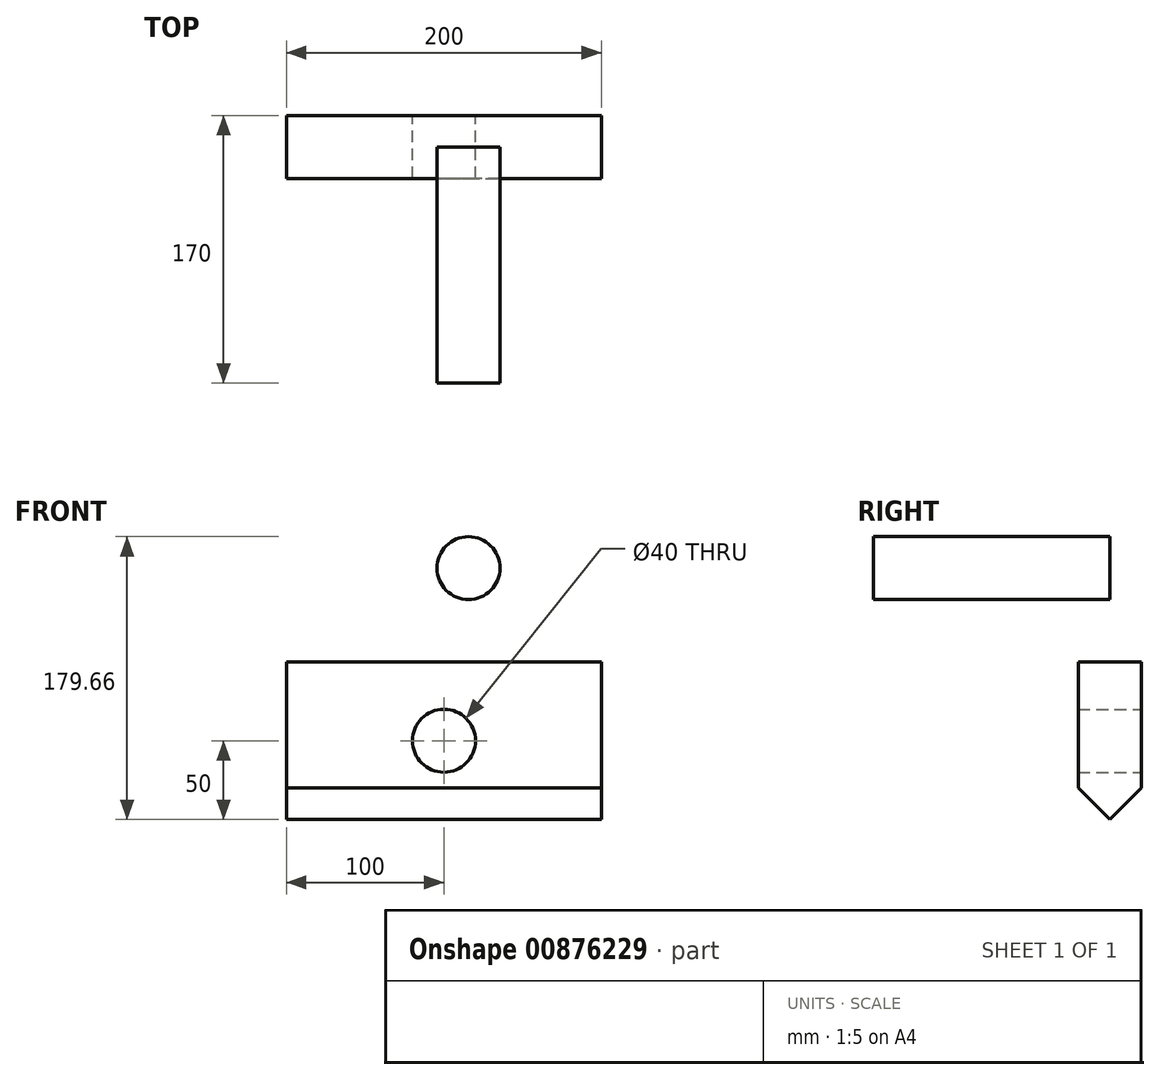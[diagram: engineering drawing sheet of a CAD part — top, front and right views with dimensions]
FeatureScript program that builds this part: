
annotation { "Feature Type Name" : "Feature", "Feature Type Description" : "" }
export const myFeature = defineFeature(function(context is Context, id is Id, definition is map)
    precondition{}
    {
        {
            var Q0;
            Q0=qCreatedBy(makeId("Front.planeOp"),FACE);
            var sketch = newSketch(context, id + "F0", { "sketchPlane" : qUnion([Q0])});
            skLineSegment(sketch, "E0.bottom", {"start": v(100, 50) * mm, "end": v(-100, 50) * mm});
            skLineSegment(sketch, "E0.top", {"start": v(100, -50) * mm, "end": v(-100, -50) * mm});
            skLineSegment(sketch, "E0.left", {"start": v(100, 50) * mm, "end": v(100, -50) * mm});
            skLineSegment(sketch, "E0.right", {"start": v(-100, 50) * mm, "end": v(-100, -50) * mm});
            skPoint(sketch, "E0.middle", {"position": v(0, 0) * mm});
            skCircle(sketch, "E1", {"center": v(0, 0) * mm, "radius": 20 * mm});
            skSolve(sketch);
        }
        {
            var Q0;
            Q0=makeQuery(id+"F0.imprint","IMPRINT",FACE,{"disambiguationData":[TD([[makeQuery(id+"F0.imprint","IMPRINT",EDGE,{"derivedFrom":sQuery(id+"F0.wireOp",EDGE,"E0.bottom")}),1.0]])]});
            extrude(context, id + "F1", {"entities" : qUnion([Q0]), "depth" : 20 * mm, "offsetDistance" : 25 * mm, "hasSecondDirection" : true, "secondDirectionOppositeDirection" : true, "secondDirectionDepth" : 20 * mm});
        }
        {
            var Q0;
            Q0=makeQuery(id+"F1.opExtrude","CAP_EDGE",EDGE,{"disambiguationData":[OSD([sQuery(id+"F0.wireOp",EDGE,"E0.top")])],"isStart":true});
            var Q1;
            Q1=makeQuery(id+"F1.opExtrude","CAP_EDGE",EDGE,{"disambiguationData":[OSD([sQuery(id+"F0.wireOp",EDGE,"E0.top")])],"isStart":false});
            chamfer(context, id + "F2", {"entities" : qUnion([Q0, Q1]), "width" : 20 * mm, "tangentPropagation" : true});
        }
        {
            var Q0;
            Q0=qCreatedBy(makeId("Front.planeOp"),FACE);
            var sketch = newSketch(context, id + "F3", { "sketchPlane" : qUnion([Q0])});
            skCircle(sketch, "E2", {"center": v(15.6, 109.66) * mm, "radius": 20 * mm});
            skSolve(sketch);
        }
        {
            var Q0;
            Q0=makeQuery(id+"F3.imprint","IMPRINT",FACE,{"disambiguationData":[TD([[makeQuery(id+"F3.imprint","IMPRINT",EDGE,{"derivedFrom":sQuery(id+"F3.wireOp",EDGE,"E2")}),1.0]])]});
            var Q1;
            Q1=sQuery(id+"F3.wireOp",EDGE,"E2");
            extrude(context, id + "F4", {"entities" : qUnion([Q0]), "surfaceEntities" : qUnion([Q1]), "depth" : 150 * mm, "offsetDistance" : 25 * mm});
        }
    });
